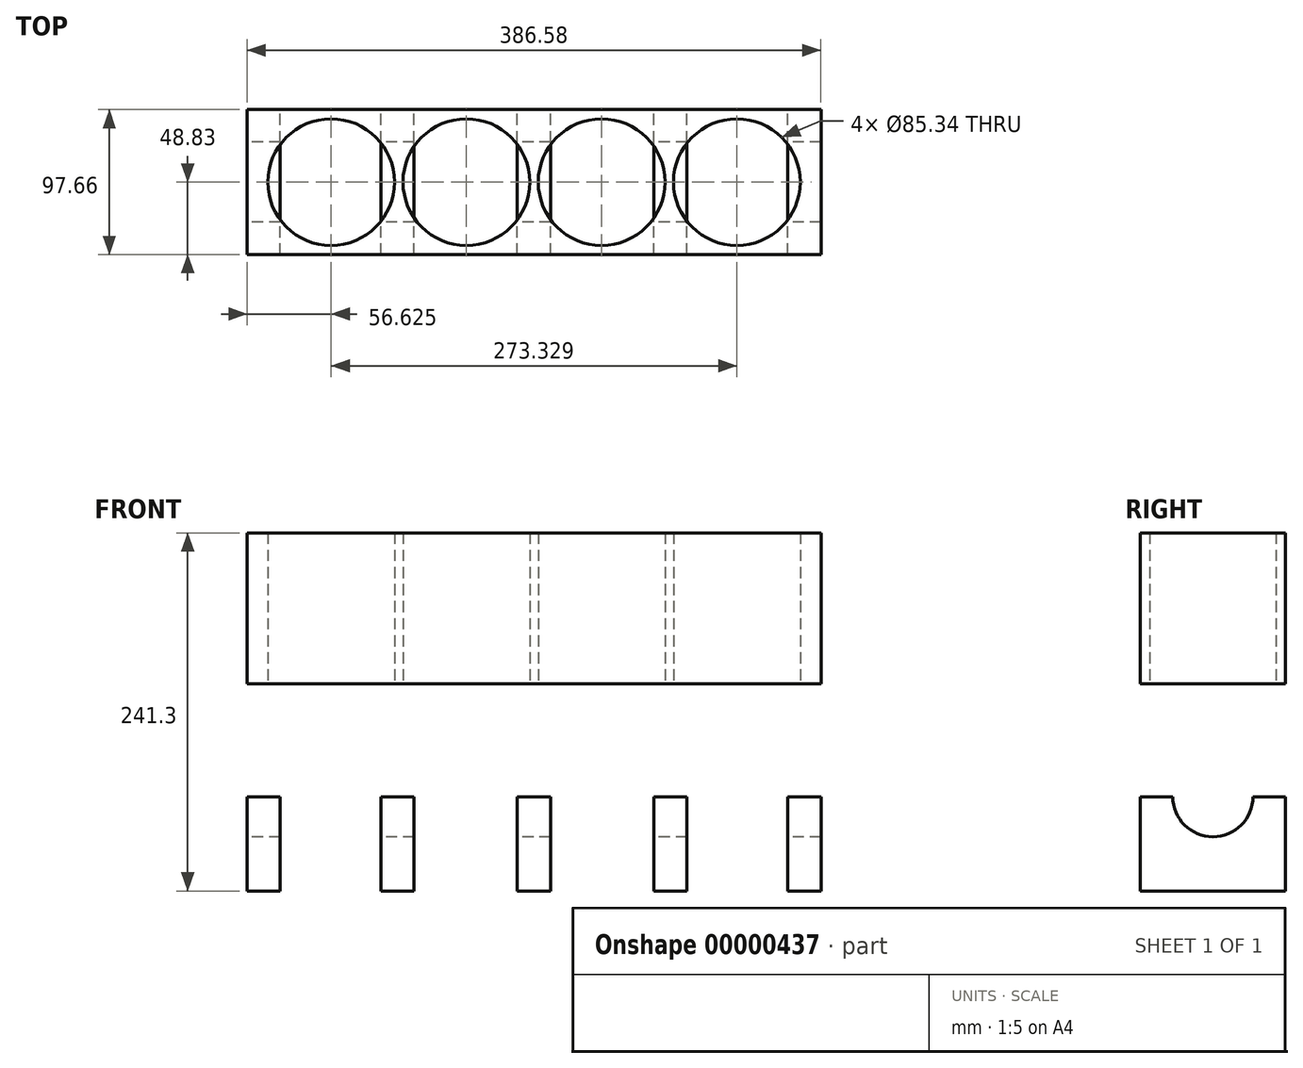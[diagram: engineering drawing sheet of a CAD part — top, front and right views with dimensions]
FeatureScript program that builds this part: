
annotation { "Feature Type Name" : "Feature", "Feature Type Description" : "" }
export const myFeature = defineFeature(function(context is Context, id is Id, definition is map)
    precondition{}
    {
        {
            var Q0;
            Q0=qCreatedBy(makeId("Front.planeOp"),FACE);
            var sketch = newSketch(context, id + "F0", { "sketchPlane" : qUnion([Q0])});
            skLineSegment(sketch, "E0.bottom", {"start": v(-193.3, 0) * mm, "end": v(-170.94, 0) * mm});
            skLineSegment(sketch, "E0.top", {"start": v(-193.3, -63.5) * mm, "end": v(-170.94, -63.5) * mm});
            skLineSegment(sketch, "E0.left", {"start": v(-193.3, 0) * mm, "end": v(-193.3, -63.5) * mm});
            skLineSegment(sketch, "E0.right", {"start": v(193.3, 0) * mm, "end": v(193.3, -63.5) * mm});
            skLineSegment(sketch, "E1", {"start": v(-170.94, 0) * mm, "end": v(-170.94, -63.5) * mm});
            skLineSegment(sketch, "E2", {"start": v(-103.05, 0) * mm, "end": v(-103.05, -63.5) * mm});
            skLineSegment(sketch, "E3", {"start": v(-80.7, 0) * mm, "end": v(-80.7, -63.5) * mm});
            skLineSegment(sketch, "E4", {"start": v(-11.18, 0) * mm, "end": v(-11.18, -63.5) * mm});
            skLineSegment(sketch, "E5", {"start": v(0, 0) * mm, "end": v(0, -63.5) * mm, "construction": true});
            skLineSegment(sketch, "E6.0.MirrorCS", {"start": v(11.18, 0) * mm, "end": v(11.18, -63.5) * mm});
            skLineSegment(sketch, "E7.0.MirrorCS", {"start": v(80.7, 0) * mm, "end": v(80.7, -63.5) * mm});
            skLineSegment(sketch, "E8.0.MirrorCS", {"start": v(103.05, 0) * mm, "end": v(103.05, -63.5) * mm});
            skLineSegment(sketch, "E9.0.MirrorCS", {"start": v(170.94, 0) * mm, "end": v(170.94, -63.5) * mm});
            skLineSegment(sketch, "E10.trimOffspring", {"start": v(-103.05, 0) * mm, "end": v(-80.7, 0) * mm});
            skLineSegment(sketch, "E11.trimOffspring", {"start": v(-103.05, -63.5) * mm, "end": v(-80.7, -63.5) * mm});
            skLineSegment(sketch, "E12.trimOffspring", {"start": v(-11.18, 0) * mm, "end": v(11.18, 0) * mm});
            skLineSegment(sketch, "E13.trimOffspring", {"start": v(-11.18, -63.5) * mm, "end": v(11.18, -63.5) * mm});
            skLineSegment(sketch, "E14.trimOffspring", {"start": v(80.7, 0) * mm, "end": v(103.05, 0) * mm});
            skLineSegment(sketch, "E15.trimOffspring", {"start": v(80.7, -63.5) * mm, "end": v(103.05, -63.5) * mm});
            skLineSegment(sketch, "E16.trimOffspring", {"start": v(170.94, 0) * mm, "end": v(193.3, 0) * mm});
            skLineSegment(sketch, "E17.trimOffspring", {"start": v(170.94, -63.5) * mm, "end": v(193.3, -63.5) * mm});
            skSolve(sketch);
        }
        {
            var Q0;
            {Q0=qUnion([makeQuery(id+"F0.imprint","IMPRINT",FACE,{"disambiguationData":[TD([[makeQuery(id+"F0.imprint","IMPRINT",EDGE,{"derivedFrom":sQuery(id+"F0.wireOp",EDGE,"E0.bottom")}),-1.0]])]}),makeQuery(id+"F0.imprint","IMPRINT",FACE,{"disambiguationData":[TD([[makeQuery(id+"F0.imprint","IMPRINT",EDGE,{"derivedFrom":sQuery(id+"F0.wireOp",EDGE,"E0.right")}),-1.0]])]}),makeQuery(id+"F0.imprint","IMPRINT",FACE,{"disambiguationData":[TD([[makeQuery(id+"F0.imprint","IMPRINT",EDGE,{"derivedFrom":sQuery(id+"F0.wireOp",EDGE,"E2")}),1.0]])]}),makeQuery(id+"F0.imprint","IMPRINT",FACE,{"disambiguationData":[TD([[makeQuery(id+"F0.imprint","IMPRINT",EDGE,{"derivedFrom":sQuery(id+"F0.wireOp",EDGE,"E4")}),1.0]])]}),makeQuery(id+"F0.imprint","IMPRINT",FACE,{"disambiguationData":[TD([[makeQuery(id+"F0.imprint","IMPRINT",EDGE,{"derivedFrom":sQuery(id+"F0.wireOp",EDGE,"E7.0.MirrorCS")}),1.0]])]})]);}
            extrude(context, id + "F1", {"entities" : qUnion([Q0]), "depth" : 97.66 * mm, "symmetric" : true});
        }
        {
            var Q0;
            Q0=makeQuery(id+"F1.opExtrude","SWEPT_FACE",FACE,{"disambiguationData":[OSD([sQuery(id+"F0.wireOp",EDGE,"E0.left")])]});
            var sketch = newSketch(context, id + "F2", { "sketchPlane" : qUnion([Q0])});
            skCircle(sketch, "E18", {"center": v(0, 0) * mm, "radius": 26.99 * mm});
            skSolve(sketch);
        }
        {
            var Q0;
            {var subQ0=makeQuery(id+"F1.opExtrude","SWEPT_EDGE",EDGE,{"disambiguationData":[OSD([sQuery(id+"F0.wireOp",EDGE,"E0.bottom"),sQuery(id+"F0.wireOp",EDGE,"E0.left")])]});var subQ1=sQuery(id+"F2.wireOp",EDGE,"E18");var subQ3=makeQuery(id+"F2.imprint","INTERSECT",VERTEX,{"disambiguationData":[OD(0.0)],"derivedFrom":[subQ0,subQ1]});Q0=qUnion([makeQuery(id+"F2.imprint","IMPRINT",FACE,{"disambiguationData":[TD([[makeQuery(id+"F2.imprint","IMPRINT",EDGE,{"disambiguationData":[TD([[subQ3,1.0]])],"derivedFrom":subQ1}),1.0]])]}),makeQuery(id+"F2.imprint","IMPRINT",FACE,{"disambiguationData":[TD([[makeQuery(id+"F2.imprint","IMPRINT",EDGE,{"disambiguationData":[TD([[subQ3,-1.0]])],"derivedFrom":subQ1}),1.0]])]})]);}
            extrude(context, id + "F3", {"entities" : qUnion([Q0]), "operationType" : NewBodyOperationType.REMOVE, "endBound" : BoundingType.THROUGH_ALL, "oppositeDirection" : true, "depth" : 25.4 * mm});
        }
        {
            var Q0;
            Q0=qCreatedBy(makeId("Top.planeOp"),FACE);
            cPlane(context, id + "F4", {"entities" : qUnion([Q0]), "cplaneType" : CPlaneType.OFFSET, "offset" : 76.2 * mm, "width" : 381 * mm, "height" : 381 * mm});
        }
        {
            var Q0;
            Q0=qCreatedBy(id+"F4.planeOp",FACE);
            var sketch = newSketch(context, id + "F5", { "sketchPlane" : qUnion([Q0])});
            skCircle(sketch, "E19", {"center": v(-45.55, 0) * mm, "radius": 42.67 * mm});
            skCircle(sketch, "E20", {"center": v(-136.66, 0) * mm, "radius": 42.67 * mm});
            skLineSegment(sketch, "E21", {"start": v(0, 48.83) * mm, "end": v(0, -48.83) * mm, "construction": true});
            skCircle(sketch, "E22.0.MirrorC", {"center": v(45.55, 0) * mm, "radius": 42.67 * mm});
            skCircle(sketch, "E23.0.MirrorC", {"center": v(136.66, 0) * mm, "radius": 42.67 * mm});
            skLineSegment(sketch, "E24.bottom", {"start": v(-193.3, 48.83) * mm, "end": v(193.3, 48.83) * mm});
            skLineSegment(sketch, "E24.top", {"start": v(-193.3, -48.83) * mm, "end": v(193.3, -48.83) * mm});
            skLineSegment(sketch, "E24.left", {"start": v(-193.3, 48.83) * mm, "end": v(-193.3, -48.83) * mm});
            skLineSegment(sketch, "E24.right", {"start": v(193.3, 48.83) * mm, "end": v(193.3, -48.83) * mm});
            skSolve(sketch);
        }
        {
            var Q0;
            Q0=makeQuery(id+"F5.imprint","IMPRINT",FACE,{"disambiguationData":[TD([[makeQuery(id+"F5.imprint","IMPRINT",EDGE,{"derivedFrom":sQuery(id+"F5.wireOp",EDGE,"E19")}),-1.0]])]});
            extrude(context, id + "F6", {"entities" : qUnion([Q0]), "depth" : 101.6 * mm});
        }
    });
